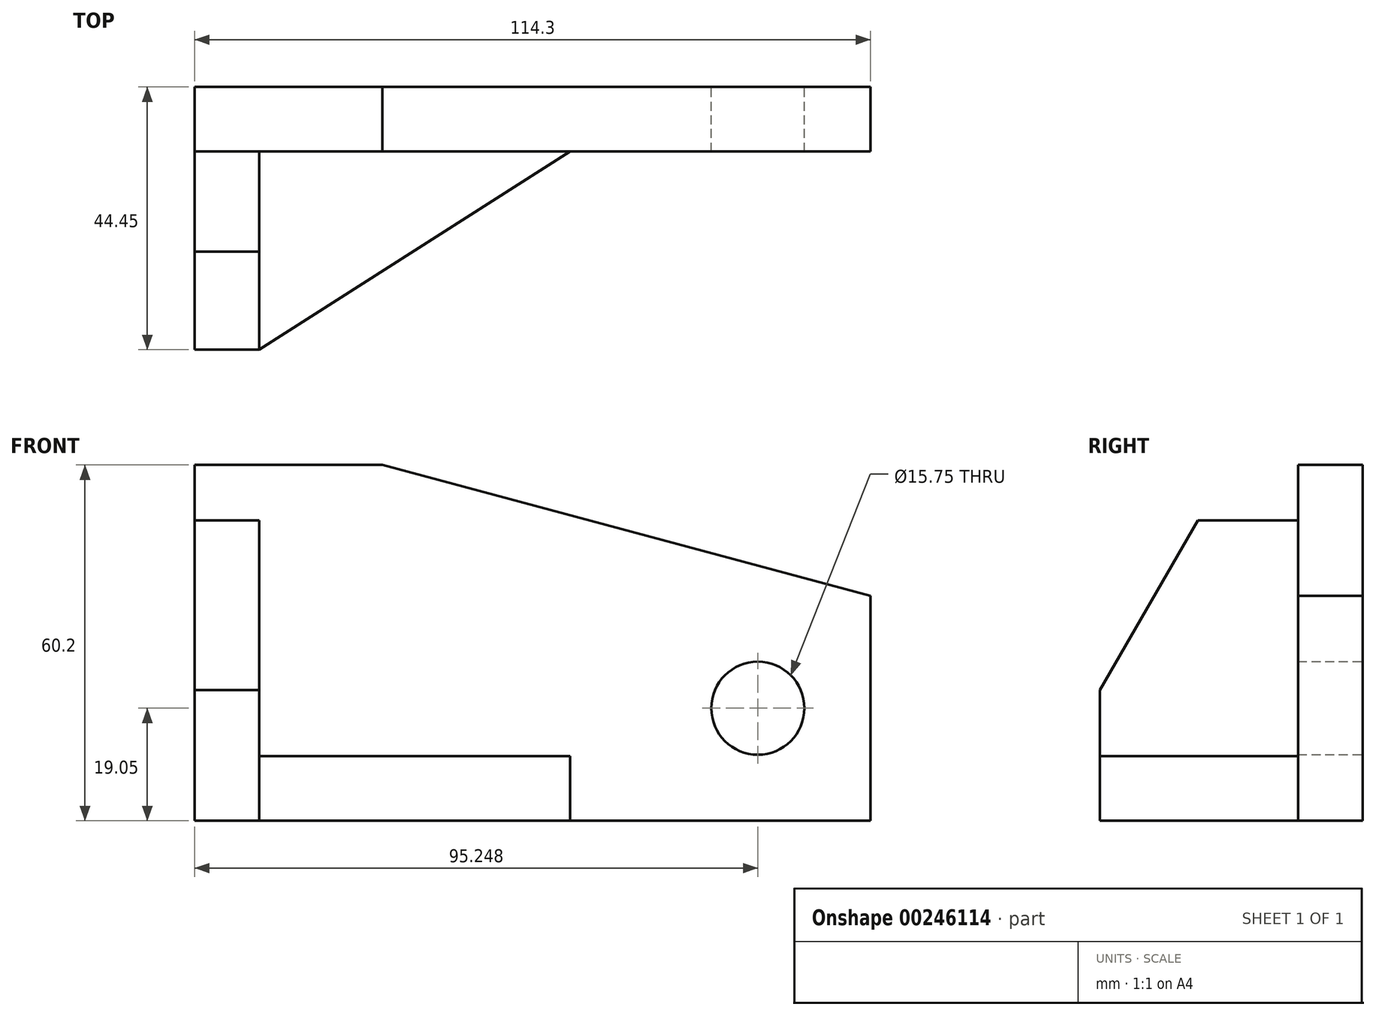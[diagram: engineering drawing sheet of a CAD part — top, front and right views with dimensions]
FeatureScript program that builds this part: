
annotation { "Feature Type Name" : "Feature", "Feature Type Description" : "" }
export const myFeature = defineFeature(function(context is Context, id is Id, definition is map)
    precondition{}
    {
        {
            var Q0;
            Q0=qCreatedBy(makeId("Front.planeOp"),FACE);
            var sketch = newSketch(context, id + "F0", { "sketchPlane" : qUnion([Q0])});
            skLineSegment(sketch, "E0", {"start": v(-59.24, 41.15) * mm, "end": v(-59.24, -19.05) * mm});
            skLineSegment(sketch, "E1", {"start": v(-59.24, -19.05) * mm, "end": v(55.06, -19.05) * mm});
            skLineSegment(sketch, "E2", {"start": v(-27.5, 41.15) * mm, "end": v(-59.24, 41.15) * mm});
            skLineSegment(sketch, "E3", {"start": v(-27.5, 41.15) * mm, "end": v(55.06, 19.03) * mm});
            skCircle(sketch, "E4", {"center": v(36, 0) * mm, "radius": 7.87 * mm});
            skLineSegment(sketch, "E5", {"start": v(55.06, 19.03) * mm, "end": v(55.06, -19.05) * mm});
            skPoint(sketch, "E6", {"position": v(55.06, 0) * mm});
            skLineSegment(sketch, "E7", {"start": v(36, 16.3) * mm, "end": v(36, -7.87) * mm, "construction": true});
            skLineSegment(sketch, "E8", {"start": v(-48.32, -19.05) * mm, "end": v(-48.32, 31.75) * mm});
            skLineSegment(sketch, "E9", {"start": v(-48.32, 31.75) * mm, "end": v(-59.24, 31.75) * mm});
            skPoint(sketch, "E10", {"position": v(4.26, -19.05) * mm});
            skLineSegment(sketch, "E11", {"start": v(4.26, -19.05) * mm, "end": v(4.26, -8.13) * mm});
            skLineSegment(sketch, "E12", {"start": v(4.26, -8.13) * mm, "end": v(-48.32, -8.13) * mm});
            skSolve(sketch);
        }
        {
            var Q0;
            {var subQ0=sQuery(id+"F0.wireOp",EDGE,"E3");Q0=makeQuery(id+"F0.imprint","IMPRINT",FACE,{"disambiguationData":[TD([[makeQuery(id+"F0.imprint","IMPRINT",EDGE,{"derivedFrom":subQ0}),-1.0]])]});}
            extrude(context, id + "F1", {"entities" : qUnion([Q0]), "depth" : 10.92 * mm});
        }
        {
            var Q0;
            {var subQ4=sQuery(id+"F0.wireOp",EDGE,"E8");Q0=makeQuery(id+"F0.imprint","IMPRINT",FACE,{"disambiguationData":[TD([[makeQuery(id+"F0.imprint","IMPRINT",EDGE,{"derivedFrom":subQ4}),1.0]])]});}
            extrude(context, id + "F2", {"entities" : qUnion([Q0]), "operationType" : NewBodyOperationType.ADD, "depth" : 44.45 * mm});
        }
        {
            var Q0;
            {var subQ3=sQuery(id+"F0.wireOp",EDGE,"E11");Q0=makeQuery(id+"F0.imprint","IMPRINT",FACE,{"disambiguationData":[TD([[makeQuery(id+"F0.imprint","IMPRINT",EDGE,{"derivedFrom":subQ3}),1.0]])]});}
            extrude(context, id + "F3", {"entities" : qUnion([Q0]), "operationType" : NewBodyOperationType.ADD, "depth" : 44.45 * mm});
        }
        {
            var Q0;
            Q0=makeQuery(id+"F3.opExtrude","SWEPT_FACE",FACE,{"disambiguationData":[OSD([sQuery(id+"F0.wireOp",EDGE,"E12")])]});
            var sketch = newSketch(context, id + "F4", { "sketchPlane" : qUnion([Q0])});
            skLineSegment(sketch, "E13", {"start": v(-48.32, -44.45) * mm, "end": v(4.26, -10.92) * mm});
            skSolve(sketch);
        }
        {
            var Q0;
            Q0=makeQuery(id+"F4.imprint","IMPRINT",FACE,{"disambiguationData":[TD([[makeQuery(id+"F4.imprint","IMPRINT",EDGE,{"derivedFrom":sQuery(id+"F4.wireOp",EDGE,"E13")}),-1.0]])]});
            extrude(context, id + "F5", {"entities" : qUnion([Q0]), "operationType" : NewBodyOperationType.REMOVE, "oppositeDirection" : true, "depth" : 25.4 * mm});
        }
        {
            var Q0;
            {var subQ0=sQuery(id+"F0.wireOp",EDGE,"E0");Q0=makeQuery(id+"F2.boolean.opBoolean","MERGE",FACE,{"derivedFrom":[makeQuery(id+"F1.opExtrude","SWEPT_FACE",FACE,{"disambiguationData":[OSD([subQ0])]}),makeQuery(id+"F2.opExtrude","SWEPT_FACE",FACE,{"disambiguationData":[OSD([subQ0])]})]});}
            var sketch = newSketch(context, id + "F6", { "sketchPlane" : qUnion([Q0])});
            skLineSegment(sketch, "E14", {"start": v(44.45, 3.05) * mm, "end": v(27.88, 31.75) * mm});
            skSolve(sketch);
        }
        {
            var Q0;
            {var subQ0=sQuery(id+"F6.wireOp",EDGE,"E14");Q0=makeQuery(id+"F6.imprint","IMPRINT",FACE,{"disambiguationData":[TD([[makeQuery(id+"F6.imprint","IMPRINT",EDGE,{"derivedFrom":subQ0}),-1.0]])]});}
            extrude(context, id + "F7", {"entities" : qUnion([Q0]), "operationType" : NewBodyOperationType.REMOVE, "oppositeDirection" : true, "depth" : 25.4 * mm});
        }
    });
